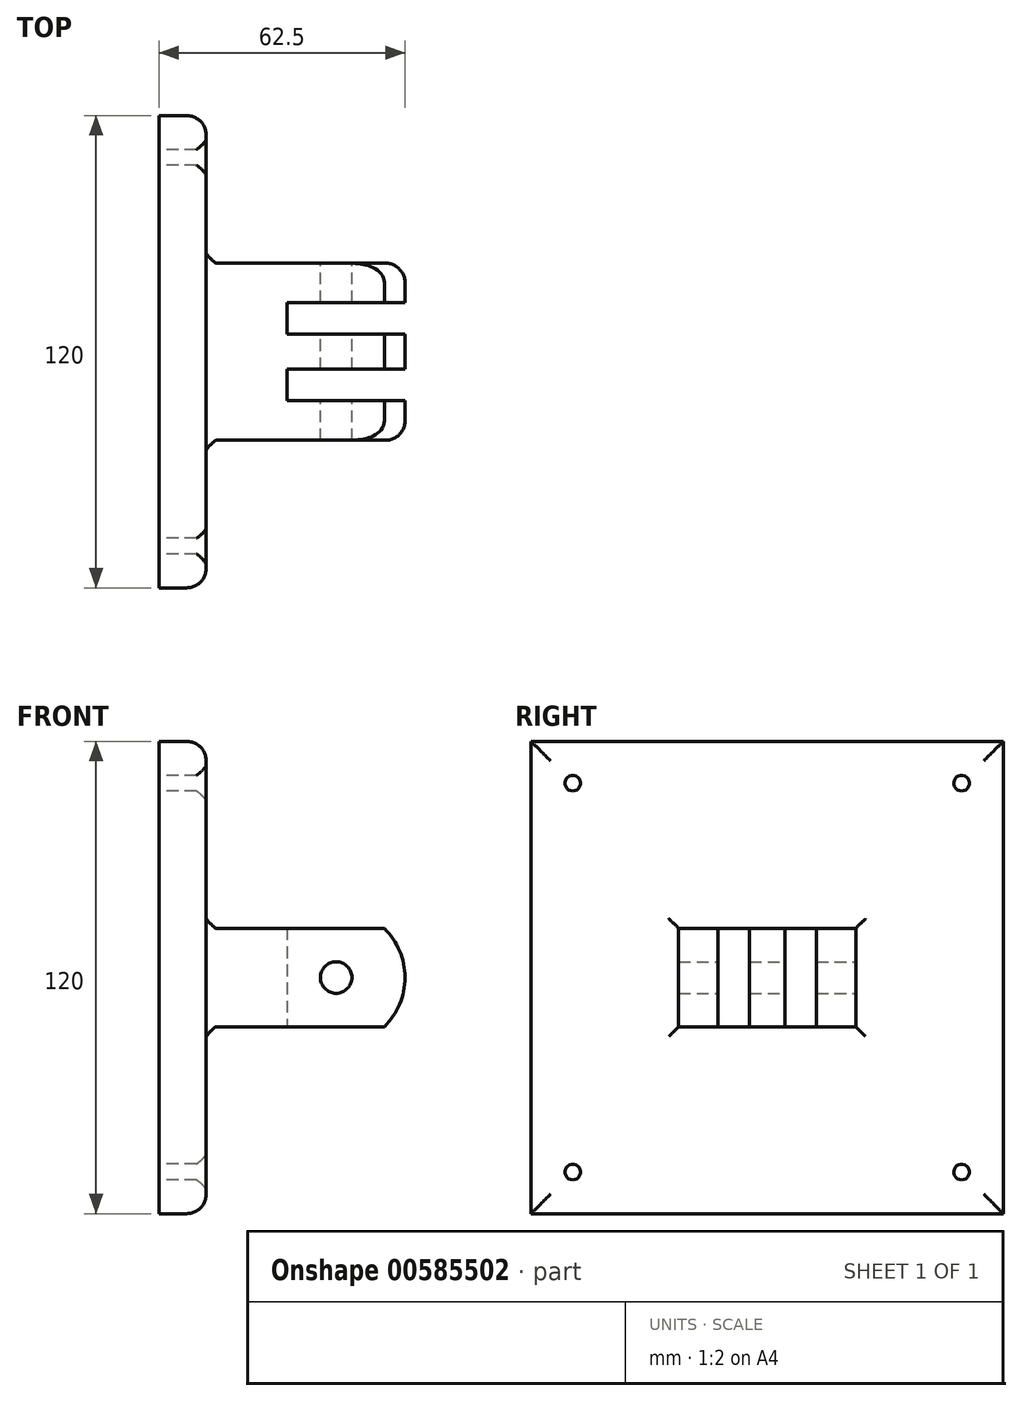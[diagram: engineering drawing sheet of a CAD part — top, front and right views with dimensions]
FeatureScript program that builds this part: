
annotation { "Feature Type Name" : "Feature", "Feature Type Description" : "" }
export const myFeature = defineFeature(function(context is Context, id is Id, definition is map)
    precondition{}
    {
        {
            var Q0;
            Q0=qCreatedBy(makeId("Front.planeOp"),FACE);
            var sketch = newSketch(context, id + "F0", { "sketchPlane" : qUnion([Q0])});
            skCircle(sketch, "E0", {"center": v(45, 0) * mm, "radius": 17.5 * mm});
            skLineSegment(sketch, "E1", {"start": v(0, 0) * mm, "end": v(45, 0) * mm, "construction": true});
            skLineSegment(sketch, "E2", {"start": v(0, 17.5) * mm, "end": v(45, 17.5) * mm});
            skLineSegment(sketch, "E3.MirrorCS", {"start": v(0, -17.5) * mm, "end": v(45, -17.5) * mm});
            skCircle(sketch, "E4", {"center": v(45, 0) * mm, "radius": 4 * mm});
            skLineSegment(sketch, "E5", {"start": v(0, -17.5) * mm, "end": v(0, 17.5) * mm});
            skSolve(sketch);
        }
        {
            var Q0;
            Q0 = qSketchRegion(id + "F0", true);
            extrude(context, id + "F1", {"entities" : qUnion([Q0]), "depth" : 45 * mm, "offsetDistance" : 25 * mm});
        }
        {
            var Q0;
            Q0=qCreatedBy(makeId("Top.planeOp"),FACE);
            var sketch = newSketch(context, id + "F2", { "sketchPlane" : qUnion([Q0])});
            skLineSegment(sketch, "E6", {"start": v(32.5, -9.98) * mm, "end": v(62.5, -9.98) * mm});
            skLineSegment(sketch, "E7.0", {"start": v(32.5, -17.98) * mm, "end": v(62.5, -17.98) * mm});
            skLineSegment(sketch, "E8", {"start": v(62.5, -9.98) * mm, "end": v(62.5, -17.98) * mm});
            skLineSegment(sketch, "E9", {"start": v(62.5, 0) * mm, "end": v(62.5, -26.96) * mm});
            skLineSegment(sketch, "E10.0", {"start": v(77.2, 32.2) * mm, "end": v(-32.2, 32.2) * mm});
            skLineSegment(sketch, "E10.1", {"start": v(77.2, -77.2) * mm, "end": v(77.2, 32.2) * mm});
            skLineSegment(sketch, "E10.2", {"start": v(-32.2, -77.2) * mm, "end": v(77.2, -77.2) * mm});
            skLineSegment(sketch, "E10.3", {"start": v(-32.2, 32.2) * mm, "end": v(-32.2, -77.2) * mm});
            skLineSegment(sketch, "E11", {"start": v(32.5, -17.98) * mm, "end": v(32.5, -9.98) * mm});
            skLineSegment(sketch, "E12", {"start": v(62.5, -26.96) * mm, "end": v(32.5, -26.96) * mm});
            skLineSegment(sketch, "E13", {"start": v(32.5, -26.96) * mm, "end": v(32.5, -34.98) * mm});
            skLineSegment(sketch, "E14", {"start": v(32.5, -34.98) * mm, "end": v(62.5, -34.98) * mm});
            skLineSegment(sketch, "E15", {"start": v(62.5, -34.98) * mm, "end": v(62.5, -26.96) * mm});
            skLineSegment(sketch, "E16.0", {"start": v(0, 0) * mm, "end": v(45, 0) * mm});
            skLineSegment(sketch, "E17.0", {"start": v(0, -45) * mm, "end": v(45, -45) * mm});
            skPoint(sketch, "E18", {"position": v(22.5, 0) * mm});
            skLineSegment(sketch, "E19", {"start": v(22.5, 0) * mm, "end": v(22.5, -45) * mm, "construction": true});
            skPoint(sketch, "E20", {"position": v(22.5, -22.5) * mm});
            skSolve(sketch);
        }
        {
            var Q0;
            Q0 = qSketchRegion(id + "F2", true);
            extrude(context, id + "F3", {"entities" : qUnion([Q0]), "operationType" : NewBodyOperationType.INTERSECT, "endBound" : BoundingType.SYMMETRIC, "depth" : 25 * mm, "offsetDistance" : 25 * mm});
        }
        {
            var Q0;
            Q0=makeQuery(id+"F3.boolean.opBoolean","INTERSECT",EDGE,{"derivedFrom":[makeQuery(id+"F1.opExtrude","CAP_FACE",FACE,{"disambiguationData":[OSD([sQuery(id+"F0.wireOp",EDGE,"SQUfFeIz-mq13-bcXV-N9m1-XyjhNYFZ3jGx"),sQuery(id+"F0.wireOp",EDGE,"E0"),sQuery(id+"F0.wireOp",EDGE,"E2"),sQuery(id+"F0.wireOp",EDGE,"E3.MirrorCS"),sQuery(id+"F0.wireOp",EDGE,"UG8isZs3-05Wx-tKQf-98uV-KwBOWGHKjBA6"),sQuery(id+"F0.wireOp",EDGE,"E4")])],"isStart":true}),makeQuery(id+"F3.boolean.toolComplement.opBoolean","COPY",FACE,{"derivedFrom":makeQuery(id+"F3.opExtrude","CAP_FACE",FACE,{"disambiguationData":[OSD([sQuery(id+"F2.wireOp",EDGE,"E6"),sQuery(id+"F2.wireOp",EDGE,"E7.0"),sQuery(id+"F2.wireOp",EDGE,"E9"),sQuery(id+"F2.wireOp",EDGE,"E10.0"),sQuery(id+"F2.wireOp",EDGE,"E10.1"),sQuery(id+"F2.wireOp",EDGE,"E10.2"),sQuery(id+"F2.wireOp",EDGE,"E10.3"),sQuery(id+"F2.wireOp",EDGE,"E11"),sQuery(id+"F2.wireOp",EDGE,"E12"),sQuery(id+"F2.wireOp",EDGE,"E13"),sQuery(id+"F2.wireOp",EDGE,"E14"),sQuery(id+"F2.wireOp",EDGE,"E15"),sQuery(id+"F2.wireOp",EDGE,"73c5898d-72c0-4f4e-a033-6dedd465d04f"),sQuery(id+"F2.wireOp",EDGE,"AE2gCUsS-4YpB-pMLK-xNPw-LiylpMOYw0R5"),sQuery(id+"F2.wireOp",EDGE,"29Ro19xf-Q7Zu-ObNw-LcLb-FyusqM1WAvgB"),sQuery(id+"F2.wireOp",EDGE,"B5osdZZn-gQE5-GkCT-ZDrQ-bQBUywbO9f20"),sQuery(id+"F2.wireOp",EDGE,"teW5vena-NARO-BmIF-j6VJ-4kTqeLASXSKU"),sQuery(id+"F2.wireOp",EDGE,"XqUBpgMi-UPac-T0Q9-J9Ia-hF9AAxpOiYm5"),sQuery(id+"F2.wireOp",EDGE,"gzTr9FI2-heJH-isbr-4onl-2wMosroxCtfP"),sQuery(id+"F2.wireOp",EDGE,"0e3LMKNz-gUGj-ifDn-7pa5-bLXgqAt3iQZw"),sQuery(id+"F2.wireOp",EDGE,"ksx0h4qa-uUZK-JVH2-eKRe-YwMkUPAmDFTI"),sQuery(id+"F2.wireOp",EDGE,"OmWtCRD3-Alp2-WJ4N-d6UF-zwBNbmMcEv39"),sQuery(id+"F2.wireOp",EDGE,"FIoNcj7u-WCcu-7BLs-mwlD-5jWwbzlNoFqZ"),sQuery(id+"F2.wireOp",EDGE,"E16.0"),sQuery(id+"F2.wireOp",EDGE,"E17.0")])],"isStart":false})})]});
            var Q1;
            Q1=makeQuery(id+"F3.boolean.opBoolean","INTERSECT",EDGE,{"derivedFrom":[makeQuery(id+"F1.opExtrude","CAP_FACE",FACE,{"disambiguationData":[OSD([sQuery(id+"F0.wireOp",EDGE,"SQUfFeIz-mq13-bcXV-N9m1-XyjhNYFZ3jGx"),sQuery(id+"F0.wireOp",EDGE,"E0"),sQuery(id+"F0.wireOp",EDGE,"E2"),sQuery(id+"F0.wireOp",EDGE,"E3.MirrorCS"),sQuery(id+"F0.wireOp",EDGE,"UG8isZs3-05Wx-tKQf-98uV-KwBOWGHKjBA6"),sQuery(id+"F0.wireOp",EDGE,"E4")])],"isStart":false}),makeQuery(id+"F3.boolean.toolComplement.opBoolean","COPY",FACE,{"derivedFrom":makeQuery(id+"F3.opExtrude","CAP_FACE",FACE,{"disambiguationData":[OSD([sQuery(id+"F2.wireOp",EDGE,"E6"),sQuery(id+"F2.wireOp",EDGE,"E7.0"),sQuery(id+"F2.wireOp",EDGE,"E9"),sQuery(id+"F2.wireOp",EDGE,"E10.0"),sQuery(id+"F2.wireOp",EDGE,"E10.1"),sQuery(id+"F2.wireOp",EDGE,"E10.2"),sQuery(id+"F2.wireOp",EDGE,"E10.3"),sQuery(id+"F2.wireOp",EDGE,"E11"),sQuery(id+"F2.wireOp",EDGE,"E12"),sQuery(id+"F2.wireOp",EDGE,"E13"),sQuery(id+"F2.wireOp",EDGE,"E14"),sQuery(id+"F2.wireOp",EDGE,"E15"),sQuery(id+"F2.wireOp",EDGE,"73c5898d-72c0-4f4e-a033-6dedd465d04f"),sQuery(id+"F2.wireOp",EDGE,"AE2gCUsS-4YpB-pMLK-xNPw-LiylpMOYw0R5"),sQuery(id+"F2.wireOp",EDGE,"29Ro19xf-Q7Zu-ObNw-LcLb-FyusqM1WAvgB"),sQuery(id+"F2.wireOp",EDGE,"B5osdZZn-gQE5-GkCT-ZDrQ-bQBUywbO9f20"),sQuery(id+"F2.wireOp",EDGE,"teW5vena-NARO-BmIF-j6VJ-4kTqeLASXSKU"),sQuery(id+"F2.wireOp",EDGE,"XqUBpgMi-UPac-T0Q9-J9Ia-hF9AAxpOiYm5"),sQuery(id+"F2.wireOp",EDGE,"gzTr9FI2-heJH-isbr-4onl-2wMosroxCtfP"),sQuery(id+"F2.wireOp",EDGE,"0e3LMKNz-gUGj-ifDn-7pa5-bLXgqAt3iQZw"),sQuery(id+"F2.wireOp",EDGE,"ksx0h4qa-uUZK-JVH2-eKRe-YwMkUPAmDFTI"),sQuery(id+"F2.wireOp",EDGE,"OmWtCRD3-Alp2-WJ4N-d6UF-zwBNbmMcEv39"),sQuery(id+"F2.wireOp",EDGE,"FIoNcj7u-WCcu-7BLs-mwlD-5jWwbzlNoFqZ"),sQuery(id+"F2.wireOp",EDGE,"E16.0"),sQuery(id+"F2.wireOp",EDGE,"E17.0")])],"isStart":false})})]});
            var Q2;
            Q2=makeQuery(id+"F3.boolean.opBoolean","INTERSECT",EDGE,{"derivedFrom":[makeQuery(id+"F1.opExtrude","CAP_FACE",FACE,{"disambiguationData":[OSD([sQuery(id+"F0.wireOp",EDGE,"SQUfFeIz-mq13-bcXV-N9m1-XyjhNYFZ3jGx"),sQuery(id+"F0.wireOp",EDGE,"E0"),sQuery(id+"F0.wireOp",EDGE,"E2"),sQuery(id+"F0.wireOp",EDGE,"E3.MirrorCS"),sQuery(id+"F0.wireOp",EDGE,"UG8isZs3-05Wx-tKQf-98uV-KwBOWGHKjBA6"),sQuery(id+"F0.wireOp",EDGE,"E4")])],"isStart":true}),makeQuery(id+"F3.boolean.toolComplement.opBoolean","COPY",FACE,{"derivedFrom":makeQuery(id+"F3.opExtrude","CAP_FACE",FACE,{"disambiguationData":[OSD([sQuery(id+"F2.wireOp",EDGE,"E6"),sQuery(id+"F2.wireOp",EDGE,"E7.0"),sQuery(id+"F2.wireOp",EDGE,"E9"),sQuery(id+"F2.wireOp",EDGE,"E10.0"),sQuery(id+"F2.wireOp",EDGE,"E10.1"),sQuery(id+"F2.wireOp",EDGE,"E10.2"),sQuery(id+"F2.wireOp",EDGE,"E10.3"),sQuery(id+"F2.wireOp",EDGE,"E11"),sQuery(id+"F2.wireOp",EDGE,"E12"),sQuery(id+"F2.wireOp",EDGE,"E13"),sQuery(id+"F2.wireOp",EDGE,"E14"),sQuery(id+"F2.wireOp",EDGE,"E15"),sQuery(id+"F2.wireOp",EDGE,"73c5898d-72c0-4f4e-a033-6dedd465d04f"),sQuery(id+"F2.wireOp",EDGE,"AE2gCUsS-4YpB-pMLK-xNPw-LiylpMOYw0R5"),sQuery(id+"F2.wireOp",EDGE,"29Ro19xf-Q7Zu-ObNw-LcLb-FyusqM1WAvgB"),sQuery(id+"F2.wireOp",EDGE,"B5osdZZn-gQE5-GkCT-ZDrQ-bQBUywbO9f20"),sQuery(id+"F2.wireOp",EDGE,"teW5vena-NARO-BmIF-j6VJ-4kTqeLASXSKU"),sQuery(id+"F2.wireOp",EDGE,"XqUBpgMi-UPac-T0Q9-J9Ia-hF9AAxpOiYm5"),sQuery(id+"F2.wireOp",EDGE,"gzTr9FI2-heJH-isbr-4onl-2wMosroxCtfP"),sQuery(id+"F2.wireOp",EDGE,"0e3LMKNz-gUGj-ifDn-7pa5-bLXgqAt3iQZw"),sQuery(id+"F2.wireOp",EDGE,"ksx0h4qa-uUZK-JVH2-eKRe-YwMkUPAmDFTI"),sQuery(id+"F2.wireOp",EDGE,"OmWtCRD3-Alp2-WJ4N-d6UF-zwBNbmMcEv39"),sQuery(id+"F2.wireOp",EDGE,"FIoNcj7u-WCcu-7BLs-mwlD-5jWwbzlNoFqZ"),sQuery(id+"F2.wireOp",EDGE,"E16.0"),sQuery(id+"F2.wireOp",EDGE,"E17.0")])],"isStart":true})})]});
            var Q3;
            Q3=makeQuery(id+"F3.boolean.opBoolean","INTERSECT",EDGE,{"derivedFrom":[makeQuery(id+"F1.opExtrude","CAP_FACE",FACE,{"disambiguationData":[OSD([sQuery(id+"F0.wireOp",EDGE,"SQUfFeIz-mq13-bcXV-N9m1-XyjhNYFZ3jGx"),sQuery(id+"F0.wireOp",EDGE,"E0"),sQuery(id+"F0.wireOp",EDGE,"E2"),sQuery(id+"F0.wireOp",EDGE,"E3.MirrorCS"),sQuery(id+"F0.wireOp",EDGE,"UG8isZs3-05Wx-tKQf-98uV-KwBOWGHKjBA6"),sQuery(id+"F0.wireOp",EDGE,"E4")])],"isStart":false}),makeQuery(id+"F3.boolean.toolComplement.opBoolean","COPY",FACE,{"derivedFrom":makeQuery(id+"F3.opExtrude","CAP_FACE",FACE,{"disambiguationData":[OSD([sQuery(id+"F2.wireOp",EDGE,"E6"),sQuery(id+"F2.wireOp",EDGE,"E7.0"),sQuery(id+"F2.wireOp",EDGE,"E9"),sQuery(id+"F2.wireOp",EDGE,"E10.0"),sQuery(id+"F2.wireOp",EDGE,"E10.1"),sQuery(id+"F2.wireOp",EDGE,"E10.2"),sQuery(id+"F2.wireOp",EDGE,"E10.3"),sQuery(id+"F2.wireOp",EDGE,"E11"),sQuery(id+"F2.wireOp",EDGE,"E12"),sQuery(id+"F2.wireOp",EDGE,"E13"),sQuery(id+"F2.wireOp",EDGE,"E14"),sQuery(id+"F2.wireOp",EDGE,"E15"),sQuery(id+"F2.wireOp",EDGE,"73c5898d-72c0-4f4e-a033-6dedd465d04f"),sQuery(id+"F2.wireOp",EDGE,"AE2gCUsS-4YpB-pMLK-xNPw-LiylpMOYw0R5"),sQuery(id+"F2.wireOp",EDGE,"29Ro19xf-Q7Zu-ObNw-LcLb-FyusqM1WAvgB"),sQuery(id+"F2.wireOp",EDGE,"B5osdZZn-gQE5-GkCT-ZDrQ-bQBUywbO9f20"),sQuery(id+"F2.wireOp",EDGE,"teW5vena-NARO-BmIF-j6VJ-4kTqeLASXSKU"),sQuery(id+"F2.wireOp",EDGE,"XqUBpgMi-UPac-T0Q9-J9Ia-hF9AAxpOiYm5"),sQuery(id+"F2.wireOp",EDGE,"gzTr9FI2-heJH-isbr-4onl-2wMosroxCtfP"),sQuery(id+"F2.wireOp",EDGE,"0e3LMKNz-gUGj-ifDn-7pa5-bLXgqAt3iQZw"),sQuery(id+"F2.wireOp",EDGE,"ksx0h4qa-uUZK-JVH2-eKRe-YwMkUPAmDFTI"),sQuery(id+"F2.wireOp",EDGE,"OmWtCRD3-Alp2-WJ4N-d6UF-zwBNbmMcEv39"),sQuery(id+"F2.wireOp",EDGE,"FIoNcj7u-WCcu-7BLs-mwlD-5jWwbzlNoFqZ"),sQuery(id+"F2.wireOp",EDGE,"E16.0"),sQuery(id+"F2.wireOp",EDGE,"E17.0")])],"isStart":true})})]});
            var Q4;
            Q4=makeQuery(id+"F1.opExtrude","CAP_EDGE",EDGE,{"disambiguationData":[OSD([sQuery(id+"F0.wireOp",EDGE,"E0")])],"isStart":true});
            var Q5;
            Q5=makeQuery(id+"F1.opExtrude","CAP_EDGE",EDGE,{"disambiguationData":[OSD([sQuery(id+"F0.wireOp",EDGE,"E0")])],"isStart":false});
            var Q6;
            Q6=makeQuery(id+"F3.boolean.opBoolean","COPY",EDGE,{"derivedFrom":makeQuery(id+"F3.boolean.toolComplement.opBoolean","COPY",EDGE,{"derivedFrom":makeQuery(id+"F3.opExtrude","SWEPT_EDGE",EDGE,{"disambiguationData":[OSD([sQuery(id+"F2.wireOp",EDGE,"29Ro19xf-Q7Zu-ObNw-LcLb-FyusqM1WAvgB"),sQuery(id+"F2.wireOp",EDGE,"E17.0")])]})})});
            var Q7;
            Q7=makeQuery(id+"F3.boolean.opBoolean","COPY",EDGE,{"derivedFrom":makeQuery(id+"F3.boolean.toolComplement.opBoolean","COPY",EDGE,{"derivedFrom":makeQuery(id+"F3.opExtrude","SWEPT_EDGE",EDGE,{"disambiguationData":[OSD([sQuery(id+"F2.wireOp",EDGE,"OmWtCRD3-Alp2-WJ4N-d6UF-zwBNbmMcEv39"),sQuery(id+"F2.wireOp",EDGE,"E16.0")])]})})});
            fillet(context, id + "F4", {"entities" : qUnion([Q0, Q1, Q2, Q3, Q4, Q5, Q6, Q7]), "radius" : 5 * mm, "tangentPropagation" : true, "allowEdgeOverflow" : false});
        }
        {
            var Q0;
            Q0=qCreatedBy(makeId("Right.planeOp"),FACE);
            var sketch = newSketch(context, id + "F5", { "sketchPlane" : qUnion([Q0])});
            skLineSegment(sketch, "E21.bottom", {"start": v(-82.5, -60) * mm, "end": v(37.5, -60) * mm});
            skLineSegment(sketch, "E21.top", {"start": v(-82.5, 60) * mm, "end": v(37.5, 60) * mm});
            skLineSegment(sketch, "E21.left", {"start": v(-82.5, -60) * mm, "end": v(-82.5, 60) * mm});
            skLineSegment(sketch, "E21.right", {"start": v(37.5, -60) * mm, "end": v(37.5, 60) * mm});
            skPoint(sketch, "E21.middle", {"position": v(-22.5, 0) * mm});
            skCircle(sketch, "E22", {"center": v(-71.9, 49.4) * mm, "radius": 2 * mm});
            skLineSegment(sketch, "E23", {"start": v(-82.5, 60) * mm, "end": v(37.5, -60) * mm, "construction": true});
            skLineSegment(sketch, "E24", {"start": v(37.5, 60) * mm, "end": v(-82.5, -60) * mm, "construction": true});
            skCircle(sketch, "E25", {"center": v(26.9, 49.4) * mm, "radius": 2 * mm});
            skCircle(sketch, "E26", {"center": v(-71.9, -49.4) * mm, "radius": 2 * mm});
            skCircle(sketch, "E27", {"center": v(26.9, -49.4) * mm, "radius": 2 * mm});
            skSolve(sketch);
        }
        {
            var Q0;
            Q0=makeQuery(id+"F5.imprint","IMPRINT",FACE,{"disambiguationData":[TD([[makeQuery(id+"F5.imprint","IMPRINT",EDGE,{"derivedFrom":sQuery(id+"F5.wireOp",EDGE,"E22")}),-1.0]])]});
            var Q1;
            Q1=makeQuery(id+"F5.imprint","IMPRINT",FACE,{"disambiguationData":[TD([[makeQuery(id+"F5.imprint","IMPRINT",EDGE,{"derivedFrom":sQuery(id+"F5.wireOp",EDGE,"E21.bottom")}),1.0]])]});
            extrude(context, id + "F6", {"entities" : qUnion([Q0, Q1]), "operationType" : NewBodyOperationType.ADD, "depth" : 12 * mm, "offsetDistance" : 25 * mm});
        }
        {
            var Q0;
            Q0=makeQuery(id+"F6.opExtrude","CAP_EDGE",EDGE,{"disambiguationData":[OSD([sQuery(id+"F5.wireOp",EDGE,"E21.top")])],"isStart":false});
            var Q1;
            Q1=makeQuery(id+"F6.opExtrude","CAP_EDGE",EDGE,{"disambiguationData":[OSD([sQuery(id+"F5.wireOp",EDGE,"E21.left")])],"isStart":false});
            var Q2;
            Q2=makeQuery(id+"F6.opExtrude","CAP_EDGE",EDGE,{"disambiguationData":[OSD([sQuery(id+"F5.wireOp",EDGE,"E21.bottom")])],"isStart":false});
            var Q3;
            Q3=makeQuery(id+"F6.opExtrude","CAP_EDGE",EDGE,{"disambiguationData":[OSD([sQuery(id+"F5.wireOp",EDGE,"E21.right")])],"isStart":false});
            fillet(context, id + "F7", {"entities" : qUnion([Q0, Q1, Q2, Q3]), "radius" : 5 * mm, "tangentPropagation" : true, "allowEdgeOverflow" : false});
        }
        {
            var Q0;
            Q0=makeQuery(id+"F6.opExtrude","CAP_FACE",FACE,{"disambiguationData":[OSD([sQuery(id+"F5.wireOp",EDGE,"E21.bottom"),sQuery(id+"F5.wireOp",EDGE,"E21.top"),sQuery(id+"F5.wireOp",EDGE,"E21.left"),sQuery(id+"F5.wireOp",EDGE,"E21.right"),sQuery(id+"F5.wireOp",EDGE,"E22"),sQuery(id+"F5.wireOp",EDGE,"E25"),sQuery(id+"F5.wireOp",EDGE,"E26"),sQuery(id+"F5.wireOp",EDGE,"E27")])],"isStart":false});
            fillet(context, id + "F8", {"entities" : qUnion([Q0]), "radius" : 2.5 * mm, "tangentPropagation" : true, "rho" : 0.1, "crossSection" : FilletCrossSection.CONIC, "allowEdgeOverflow" : false});
        }
    });
